# Revit family: 2080095(n0300)
name_source: partatom
category: Security Devices
units: mm (PartAtom-declared; Revit-internal decimal feet)

## family parameters
Always vertical = No
Cut with Voids When Loaded = No
Host = Ceiling
OmniClass Number = 23.85.30.14
OmniClass Title = Presence Detection/Registration
Room Calculation Point = No
Shared = Yes

## types (2) — shared parameters
zero-valued in all types: A

## per-type parameters (varying)
- Type 1: CTN=0; EF000008=0 mm  [stored 0 ft]; EF000040=0 mm  [stored 0 ft]; EF000049=0 mm  [stored 0 ft]; EF000194=0; EF000218=0 mm  [stored 0 ft]; EF000551=0 mm  [stored 0 ft]; EF000846=0 mm  [stored 0 ft]; EF000943=0 mm  [stored 0 ft]; EF001322=0 mm  [stored 0 ft]; EF001323=0 mm  [stored 0 ft]; EF003843=0 mm  [stored 0 ft]; EF003882=0; EF004101=0.00°; EF004265=0 mm  [stored 0 ft]; EF006589=0; EF006590=0; EF008011=0 mm  [stored 0 ft]; EF010517=0 mm  [stored 0 ft]; EF010886=0 mm  [stored 0 ft]; EF010945=0 mm  [stored 0 ft]; EF010946=0 mm  [stored 0 ft]; EF012278=0 mm  [stored 0 ft]; EF012569=0; LOG=0; NOCUPEROU=0; PRICEQUANTITY=0; QUANTITYINT=0; QUANTITYMIN=0
- 2080095: ARTICLENO=NB; BOMINFO=LINA; CATALOG=Theben; COO=HU; CTN=85365080; DEEPLINK_PRODUKTSEITE=http://www.theben.de; DESCLONG=Passive infrared presence detector as basic article for the DALI-2 Room Solution, for ceiling mounting flush-mounted, DALI-2 certified, Circular detection area 360°, Diameter 24 m, (452 m2) at 3 m mounting height, DALI-2 addressable up to 4 channels of light, Evaluates the information of the DALI pushbutton interfaces and controls the actuators such as DALI ECGs or DALI relays according to the DALI-2 standard, Color temperature control based on the time of day HCL (Human Centric Lighting), Operation with RGBW light sources, Time-controlled actions via integrated timer, Flexible assignment of up to 4 lighting groups, additionally up to 4 switching groups and 2 presence groups via app remote control, Constant light control or dimmable lighting in switching mode with and without daylight influence, Orientation light, switching mode and constant light control without presence influence, Adaptive 3 channel light measurement. Functions DALI-2 Room Solution: The DALI-2 Room Solution is a DALI-2 single room solution that handles all aspects of lighting control, compared to DALI presence detectors, the DALI-2 Room Solution offers new functionalities such as HCL function, TW/RGB functionality, time-controlled functions and more, for the single room solution all key components (presence detector, switching actuator, pushbutton interface) and the app for commissioning are available from one source; DESCSHORT=DALI presence detector ceiling-mounted flush-mounted, detection range 24 m, for DALI-2 Room Solution; EF000003=EV000383; EF000007=White; EF000008=110 mm  [stored 0.360892 ft]; EF000010=Presence detector; EF000025=false; EF000040=83 mm  [stored 0.27231 ft]; EF000049=110 mm  [stored 0.360892 ft]; EF000124=Screw clamp; EF000139=Untreated; EF000147=false; EF000187=AC; EF000194=3600; EF000218=37 mm  [stored 0.121391 ft]; EF000416=50, 50 Hz; EF000483=false; EF000551=110 mm  [stored 0.360892 ft]; EF000846=48 mm  [stored 0.15748 ft]; EF000943=48 mm  [stored 0.15748 ft]; EF001098=true; EF001099=false; EF001198=false; EF001257=Thermoplast; EF001322=12000 mm; EF001323=12000 mm; EF001731=-15, 45 °C; EF002169=Plastic; EF003429=true; EF003808=false; EF003814=10, 3000 lx; EF003832=false; EF003843=24000 mm; EF003848=true; EF003858=false; EF003863=true; EF003876=true; EF003882=9010; EF003890=false; EF003898=true; EF003904=true; EF003920=false; EF004101=360.00°; EF004265=48 mm  [stored 0.15748 ft]; EF004293=IK04; EF005474=IP54; EF005624=false; EF006243=false; EF006311=false; EF006569=matt; EF006582=0, 360 °; EF006589=10; EF006590=60; EF006644=false; EF007575=true; EF008011=2500 mm  [stored 8.2021 ft]; EF009569=true; EF010517=46 mm  [stored 0.150919 ft]; EF010886=30 mm  [stored 0.0984252 ft]; EF010945=110 mm  [stored 0.360892 ft]; EF010946=65 mm  [stored 0.213255 ft]; EF011072=false; EF011991=false; EF012278=46 mm  [stored 0.150919 ft]; EF012569=38; EF014925=false; EF014926=false; EF014927=false; EF020270=Passive infrared; EF021180=true; EF023790=false; GEBRAUCHSANLEITUNG=http://www.theben.de; INTNO=4003468200391; LINA=2080095; LOG=300; MANUID=2080095; MANUNAME=Theben AG; MANUTYPEDESC=theRonda P360 DALI-2 HCL UP WH; Manufacturer=Theben; Model=2080095; NB=2080095(N0300); NBSYN=$MANUID.($SA.$A.$LOG.); NN=theRonda P DALI HCL; NOCUPEROU=1; PRICEQUANTITY=1; PRODUKTDATENBLATT=http://www.theben.de; QUANTITYINT=1; QUANTITYMIN=1; REACH_ERKLAERUNG=http://www.theben.de; REMARKS=ERP-GROUP 347; SA=None; SUPPLIER=THEBEN; SUPPLIERALTNO=2080095

note: [stored X ft] marks values corroborated as IEEE doubles in the binary element streams (Revit-internal decimal feet)

## geometry (parser evidence)
native form markers: Sweep x13
no freeform markers — native parametric forms only
